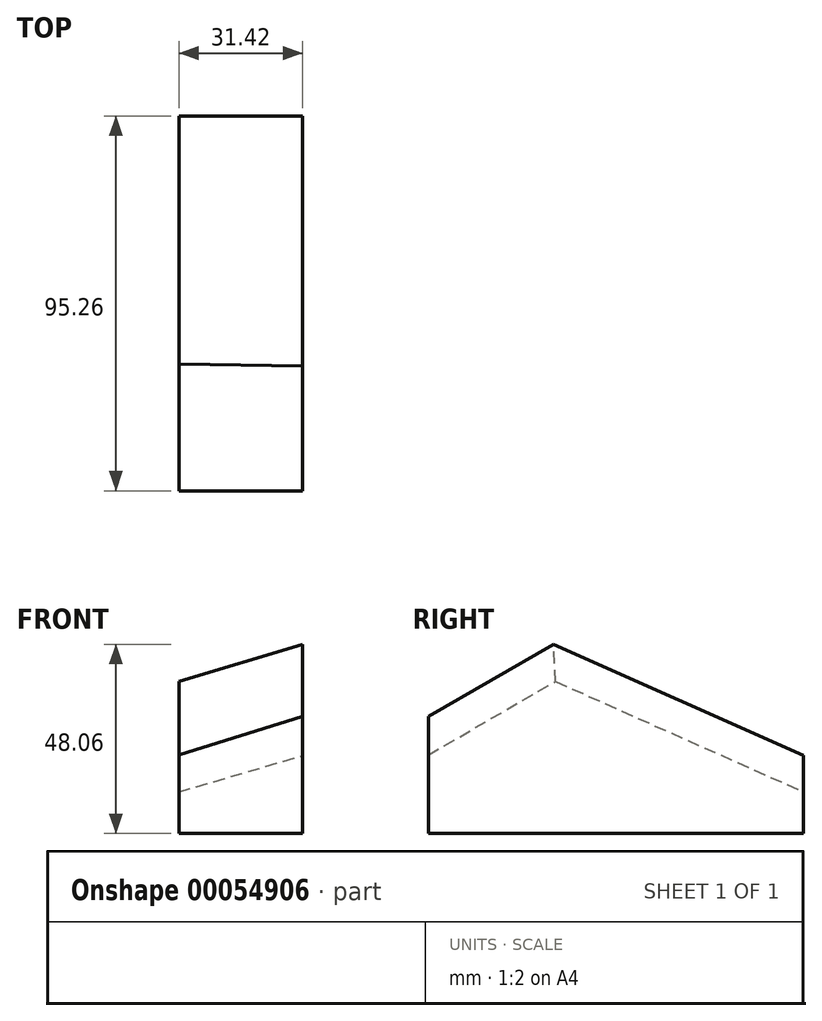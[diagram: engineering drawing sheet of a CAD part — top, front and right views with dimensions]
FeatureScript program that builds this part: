
annotation { "Feature Type Name" : "Feature", "Feature Type Description" : "" }
export const myFeature = defineFeature(function(context is Context, id is Id, definition is map)
    precondition{}
    {
        {
            var Q0;
            Q0=qCreatedBy(makeId("Front.planeOp"),FACE);
            var sketch = newSketch(context, id + "F0", { "sketchPlane" : qUnion([Q0])});
            skLineSegment(sketch, "E0.rect.bottom", {"start": v(-15.7, 25.4) * mm, "end": v(15.7, 25.4) * mm});
            skLineSegment(sketch, "E0.rect.top", {"start": v(-15.7, -25.4) * mm, "end": v(15.7, -25.4) * mm});
            skLineSegment(sketch, "E0.rect.left", {"start": v(-15.7, 25.4) * mm, "end": v(-15.7, -25.4) * mm});
            skLineSegment(sketch, "E0.rect.right", {"start": v(15.7, 25.4) * mm, "end": v(15.7, -25.4) * mm});
            skPoint(sketch, "E0.rect.middle", {"position": v(0, 0) * mm});
            skSolve(sketch);
        }
        {
            var Q0;
            Q0=makeQuery(id+"F0.imprint","IMPRINT",FACE,{"disambiguationData":[TD([[makeQuery(id+"F0.imprint","IMPRINT",EDGE,{"derivedFrom":sQuery(id+"F0.wireOp",EDGE,"E0.rect.bottom")}),-1.0]])]});
            extrude(context, id + "F1", {"entities" : qUnion([Q0]), "depth" : 95.25 * mm, "symmetric" : true});
        }
        {
            var Q0;
            Q0=makeQuery(id+"F1.opExtrude","CAP_EDGE",EDGE,{"disambiguationData":[OSD([sQuery(id+"F0.wireOp",EDGE,"E0.rect.bottom")])],"isStart":true});
            chamfer(context, id + "F2", {"entities" : qUnion([Q0]), "chamferType" : ChamferType.OFFSET_ANGLE, "width" : 30.48 * mm, "oppositeDirection" : false, "angle" : 66 * degree});
        }
        {
            var Q0;
            {var subQ0=sQuery(id+"F0.wireOp",EDGE,"E0.rect.bottom");Q0=makeQuery(id+"F2.opChamfer","BLEND_EDGE",EDGE,{"blendedFrom":[makeQuery(id+"F1.opExtrude","CAP_EDGE",EDGE,{"disambiguationData":[OSD([subQ0])],"isStart":true}),makeQuery(id+"F1.opExtrude","CAP_FACE",FACE,{"disambiguationData":[OSD([subQ0,sQuery(id+"F0.wireOp",EDGE,"E0.rect.top"),sQuery(id+"F0.wireOp",EDGE,"E0.rect.left"),sQuery(id+"F0.wireOp",EDGE,"E0.rect.right")])],"isStart":false})],"blendedInto":[makeQuery(id+"F1.opExtrude","CAP_FACE",FACE,{"disambiguationData":[OSD([subQ0,sQuery(id+"F0.wireOp",EDGE,"E0.rect.top"),sQuery(id+"F0.wireOp",EDGE,"E0.rect.left"),sQuery(id+"F0.wireOp",EDGE,"E0.rect.right")])],"isStart":false})]});}
            var Q1;
            Q1=makeQuery(id+"F1.opExtrude","CAP_EDGE",EDGE,{"disambiguationData":[OSD([sQuery(id+"F0.wireOp",EDGE,"E0.rect.bottom")])],"isStart":false});
            chamfer(context, id + "F3", {"entities" : qUnion([Q0, Q1]), "chamferType" : ChamferType.OFFSET_ANGLE, "width" : 35.56 * mm, "oppositeDirection" : false, "angle" : 30 * degree, "tangentPropagation" : true});
        }
        {
            var Q0;
            Q0=makeQuery(id+"F3.opChamfer","BLEND_EDGE",EDGE,{"blendedFrom":[makeQuery(id+"F1.opExtrude","CAP_EDGE",EDGE,{"disambiguationData":[OSD([sQuery(id+"F0.wireOp",EDGE,"E0.rect.bottom")])],"isStart":false}),makeQuery(id+"F1.opExtrude","SWEPT_FACE",FACE,{"disambiguationData":[OSD([sQuery(id+"F0.wireOp",EDGE,"E0.rect.left")])]})],"blendedInto":[makeQuery(id+"F1.opExtrude","SWEPT_FACE",FACE,{"disambiguationData":[OSD([sQuery(id+"F0.wireOp",EDGE,"E0.rect.left")])]})]});
            var Q1;
            Q1=makeQuery(id+"F2.opChamfer","BLEND_EDGE",EDGE,{"blendedFrom":[makeQuery(id+"F1.opExtrude","CAP_EDGE",EDGE,{"disambiguationData":[OSD([sQuery(id+"F0.wireOp",EDGE,"E0.rect.bottom")])],"isStart":true}),makeQuery(id+"F1.opExtrude","SWEPT_FACE",FACE,{"disambiguationData":[OSD([sQuery(id+"F0.wireOp",EDGE,"E0.rect.left")])]})],"blendedInto":[makeQuery(id+"F1.opExtrude","SWEPT_FACE",FACE,{"disambiguationData":[OSD([sQuery(id+"F0.wireOp",EDGE,"E0.rect.left")])]})]});
            chamfer(context, id + "F4", {"entities" : qUnion([Q0, Q1]), "chamferType" : ChamferType.OFFSET_ANGLE, "width" : 8.9 * mm, "oppositeDirection" : false, "angle" : 75 * degree, "tangentPropagation" : true});
        }
    });
